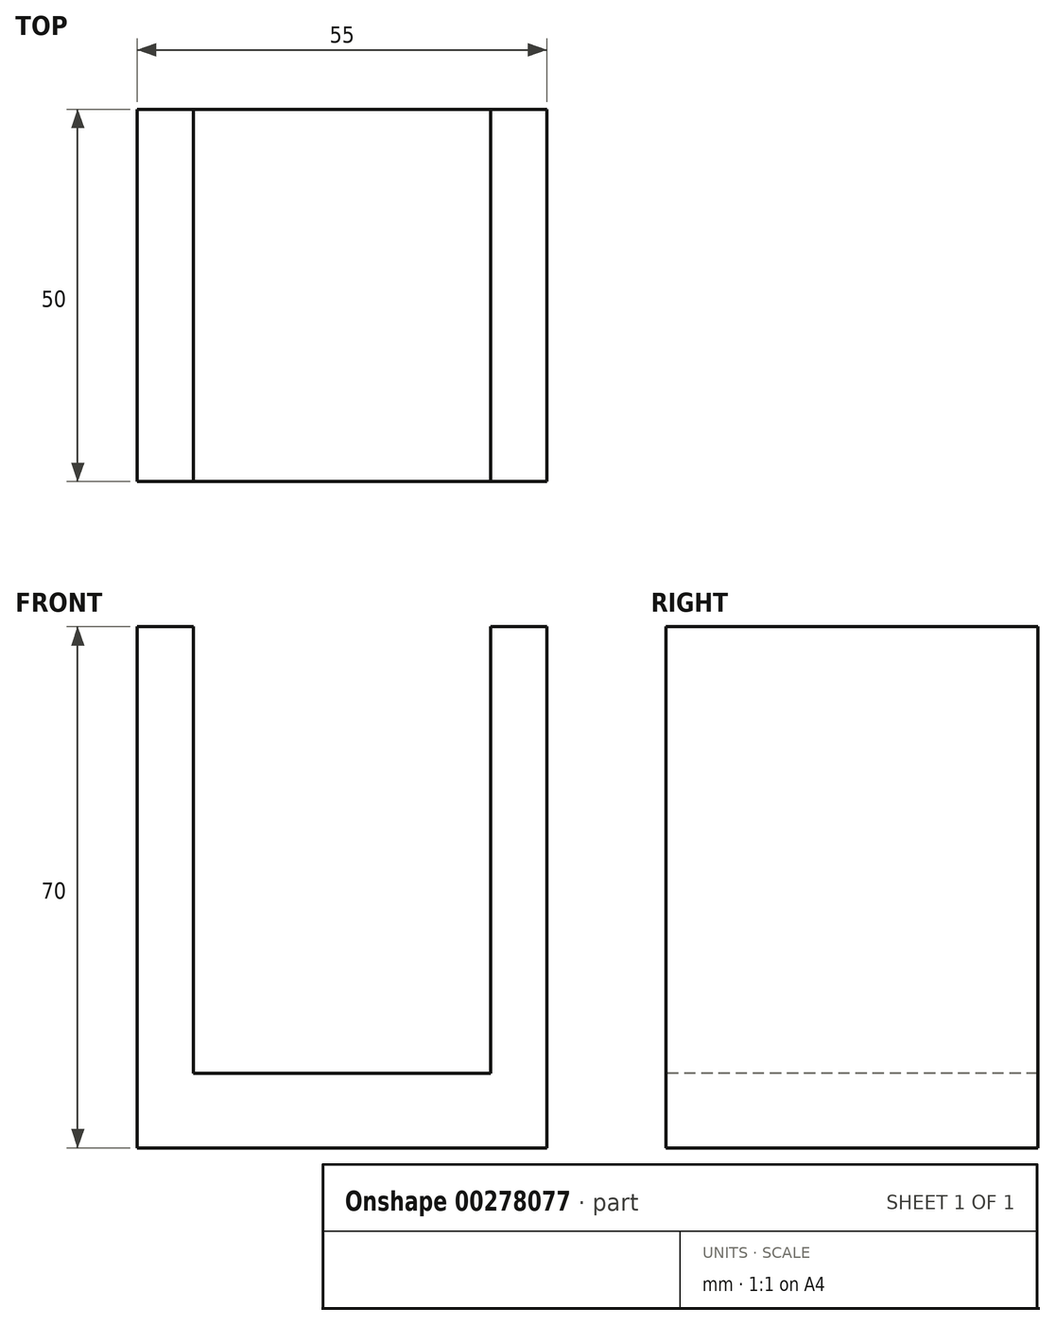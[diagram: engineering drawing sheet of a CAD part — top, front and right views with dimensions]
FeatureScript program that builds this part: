
annotation { "Feature Type Name" : "Feature", "Feature Type Description" : "" }
export const myFeature = defineFeature(function(context is Context, id is Id, definition is map)
    precondition{}
    {
        {
            var Q0;
            Q0=qCreatedBy(makeId("Top.planeOp"),FACE);
            var sketch = newSketch(context, id + "F0", { "sketchPlane" : qUnion([Q0])});
            skLineSegment(sketch, "E0.bottom", {"start": v(27.5, 25) * mm, "end": v(-27.5, 25) * mm});
            skLineSegment(sketch, "E0.top", {"start": v(27.5, -25) * mm, "end": v(-27.5, -25) * mm});
            skLineSegment(sketch, "E0.left", {"start": v(27.5, 25) * mm, "end": v(27.5, -25) * mm});
            skLineSegment(sketch, "E0.right", {"start": v(-27.5, 25) * mm, "end": v(-27.5, -25) * mm});
            skPoint(sketch, "E0.middle", {"position": v(0, 0) * mm});
            skSolve(sketch);
        }
        {
            var Q0;
            Q0=makeQuery(id+"F0.imprint","IMPRINT",FACE,{"disambiguationData":[TD([[makeQuery(id+"F0.imprint","IMPRINT",EDGE,{"derivedFrom":sQuery(id+"F0.wireOp",EDGE,"E0.bottom")}),1.0]])]});
            extrude(context, id + "F1", {"entities" : qUnion([Q0]), "depth" : 10 * mm});
        }
        {
            var Q0;
            Q0=makeQuery(id+"F1.opExtrude","CAP_FACE",FACE,{"disambiguationData":[OSD([sQuery(id+"F0.wireOp",EDGE,"E0.bottom"),sQuery(id+"F0.wireOp",EDGE,"E0.top"),sQuery(id+"F0.wireOp",EDGE,"E0.left"),sQuery(id+"F0.wireOp",EDGE,"E0.right")])],"isStart":false});
            var sketch = newSketch(context, id + "F2", { "sketchPlane" : qUnion([Q0])});
            skLineSegment(sketch, "E1", {"start": v(20, 25) * mm, "end": v(20, -25) * mm});
            skLineSegment(sketch, "E2", {"start": v(20, 25) * mm, "end": v(27.5, 25) * mm});
            skLineSegment(sketch, "E3", {"start": v(27.5, 25) * mm, "end": v(27.5, -25) * mm});
            skLineSegment(sketch, "E4", {"start": v(27.5, -25) * mm, "end": v(20, -25) * mm});
            skLineSegment(sketch, "E5.MirrorCS", {"start": v(-20, 25) * mm, "end": v(-20, -25) * mm});
            skLineSegment(sketch, "E6.MirrorCS", {"start": v(-20, 25) * mm, "end": v(-27.5, 25) * mm});
            skLineSegment(sketch, "E7.MirrorCS", {"start": v(-27.5, 25) * mm, "end": v(-27.5, -25) * mm});
            skLineSegment(sketch, "E8.MirrorCS", {"start": v(-27.5, -25) * mm, "end": v(-20, -25) * mm});
            skSolve(sketch);
        }
        {
            var Q0;
            Q0 = qSketchRegion(id + "F2", true);
            extrude(context, id + "F3", {"entities" : qUnion([Q0]), "operationType" : NewBodyOperationType.ADD, "depth" : 60 * mm});
        }
    });
